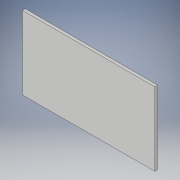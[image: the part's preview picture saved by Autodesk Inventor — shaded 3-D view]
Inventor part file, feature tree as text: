
AUTODESK INVENTOR PART (.ipt)
format: ipt  version: 2019 (Build 230136000, 136)  size: 89,088 bytes
history: native  units: in
note: dims shown in document units (in); Inventor stores cm internally (conversion verified against a paired STEP export)
features: extrude x1, sketch x1
ambient origin geometry x8: Origin, YZ Plane, XZ Plane, XY Plane, X Axis, Y Axis, Z Axis, Center Point
bodies: Solid1 (feature_tree)
feature tree (2):
  extrude  "Extrusion1"  Depth=10.2362in
  sketch  "Sketch1"  dims[d0=18.5039in d1=10.2362in d2=0.3937in d3=0.0in]
